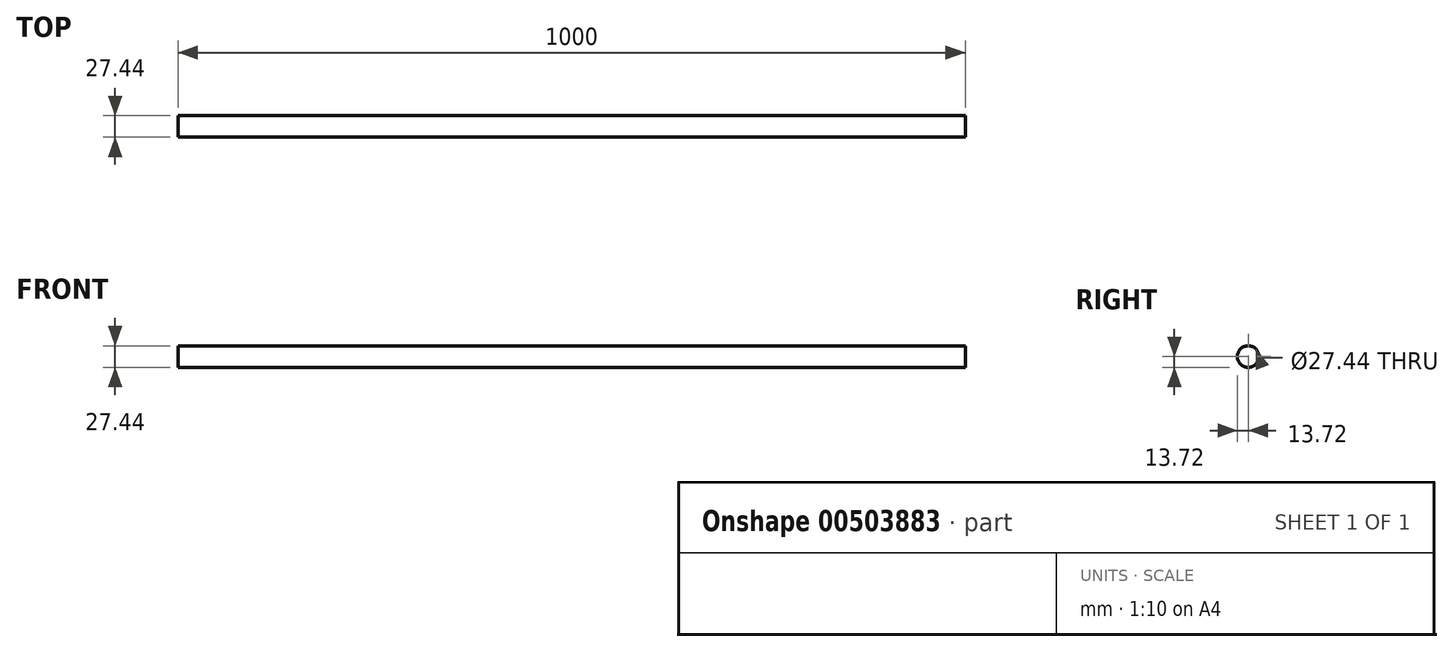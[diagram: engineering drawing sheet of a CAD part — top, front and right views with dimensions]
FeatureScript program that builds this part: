
annotation { "Feature Type Name" : "Feature", "Feature Type Description" : "" }
export const myFeature = defineFeature(function(context is Context, id is Id, definition is map)
    precondition{}
    {
        {
            var Q0;
            Q0=qCreatedBy(makeId("Right.planeOp"),FACE);
            var sketch = newSketch(context, id + "F0", { "sketchPlane" : qUnion([Q0])});
            skCircle(sketch, "E0", {"center": v(0, 0) * mm, "radius": 13.72 * mm});
            skSolve(sketch);
        }
        {
            var Q0;
            Q0=sQuery(id+"F0.wireOp",EDGE,"E0");
            extrude(context, id + "F1", {"bodyType" : ToolBodyType.SURFACE, "surfaceEntities" : qUnion([Q0]), "oppositeDirection" : true, "depth" : 1000 * mm});
        }
    });
